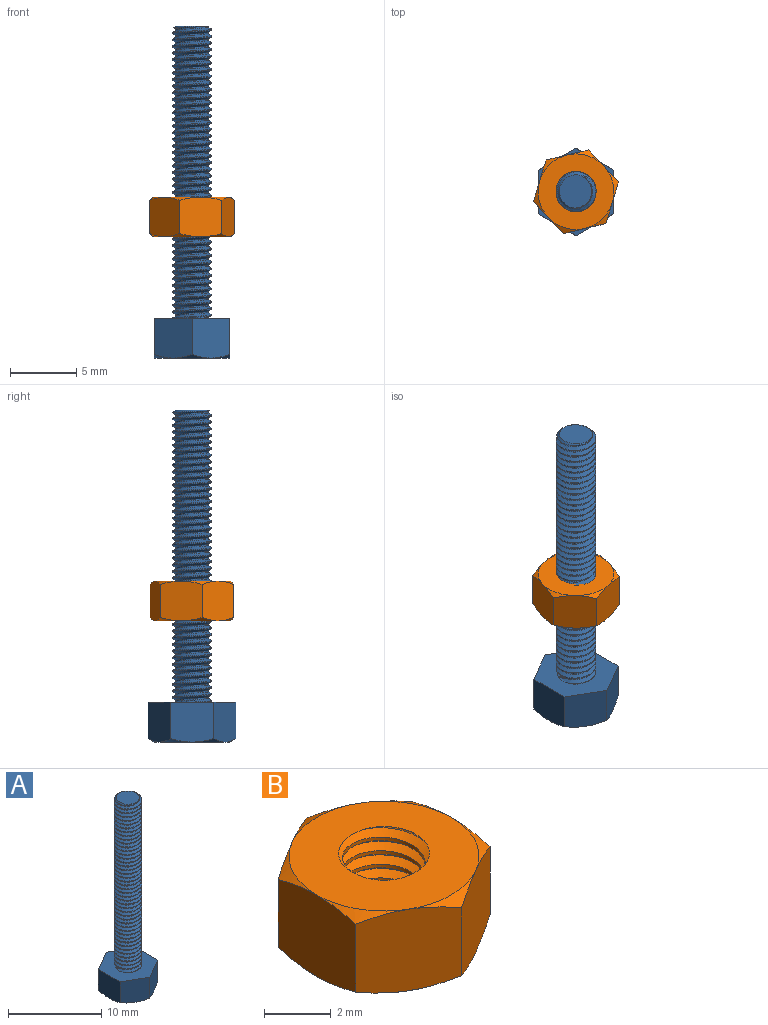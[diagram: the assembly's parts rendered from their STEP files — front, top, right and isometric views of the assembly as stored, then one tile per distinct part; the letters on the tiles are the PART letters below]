
ASSEMBLY  parts=2 mates=1
PART A: 20 faces, bbox 6.8x6.8x25.4 mm
  f0: cylinder r=1.5mm len=21.78mm, axis (0,0,-1), area -58.4mm2, adj f8,f17,f18,f19
  f1: plane 3.23x3.08mm, normal (0.5,0.87,0), area 9.6mm2, adj f2,f6,f7,f8,f10,f15
  f2: plane 3.23x3.08mm, normal (-0.5,0.86,0), area 9.6mm2, adj f1,f3,f7,f8,f14,f15
  f3: plane 3.52x3.23mm, normal (-1,0,0), area 9.6mm2, adj f2,f4,f7,f8,f13,f14
  f4: plane 3.23x3.08mm, normal (-0.5,-0.87,0), area 9.6mm2, adj f3,f5,f7,f8,f12,f13
  f5: plane 3.23x3.08mm, normal (0.5,-0.86,0), area 9.6mm2, adj f4,f6,f7,f8,f11,f12
  f6: plane 3.52x3.23mm, normal (1,0,0), area 9.6mm2, adj f1,f5,f7,f8,f10,f11
  f7: plane 5.71x5.7mm, normal (0,0,-1), area 25.6mm2, adj f1,f2,f3,f4,f5,f6,f10,f11
  f8: plane 6.72x5.85mm, normal (0,0,1), area 22.4mm2, adj f0,f1,f2,f3,f4,f5,f6,f16
  f9: plane 2.51x2.47mm, normal (0,0,1), area 4.8mm2, adj f16,f17,f18,f19
  f10: cone r=5.01mm half-angle=60deg, axis (0,0,1), area 0.7mm2, adj f1,f6,f7
  f11: cone r=5.01mm half-angle=60deg, axis (0,0,1), area 0.7mm2, adj f5,f6,f7
  f12: cone r=5.01mm half-angle=60deg, axis (0,0,1), area 0.7mm2, adj f4,f5,f7
  f13: cone r=5.01mm half-angle=60deg, axis (0,0,1), area 0.7mm2, adj f3,f4,f7
  f14: cone r=5.01mm half-angle=60deg, axis (0,0,1), area 0.7mm2, adj f2,f3,f7
  f15: cone r=5.01mm half-angle=60deg, axis (0,0,1), area 0.7mm2, adj f1,f2,f7
  f16: bspline ~22.38x2.84mm, area 46.8mm2, adj f8,f9,f17,f18
  f17: bspline ~22.41x3.46mm, area 117.7mm2, adj f0,f8,f9,f16,f19
  f18: bspline ~22.24x3.46mm, area 117.8mm2, adj f0,f8,f9,f16,f19
  f19: cone r=1.5mm half-angle=49.1deg, axis (0,0,-1), area 1.2mm2, adj f0,f9,f17,f18
PART B: 24 faces, bbox 6.9x6.9x3.7 mm
  f0: plane 5.84x5.84mm, normal (0,0,1), area 19.6mm2, adj f4,f5,f7,f9,f11,f13,f20,f21
  f1: plane 5.84x5.84mm, normal (0,0,-1), area 19.6mm2, adj f2,f3,f6,f8,f10,f12,f20,f21
  f2: cone r=2.85mm half-angle=60deg, axis (0,0,1), area 0.8mm2, adj f1,f14,f15
  f3: cone r=2.85mm half-angle=60deg, axis (0,0,1), area 0.8mm2, adj f1,f14,f19
  f4: cone r=2.85mm half-angle=60deg, axis (0,0,-1), area 0.8mm2, adj f0,f14,f15
  f5: cone r=2.85mm half-angle=60deg, axis (0,0,-1), area 0.8mm2, adj f0,f14,f19
  f6: cone r=2.85mm half-angle=60deg, axis (0,0,1), area 0.8mm2, adj f1,f15,f16
  f7: cone r=2.85mm half-angle=60deg, axis (0,0,-1), area 0.8mm2, adj f0,f15,f16
  f8: cone r=2.85mm half-angle=60deg, axis (0,0,1), area 0.8mm2, adj f1,f16,f17
  f9: cone r=2.85mm half-angle=60deg, axis (0,0,-1), area 0.8mm2, adj f0,f16,f17
  f10: cone r=2.85mm half-angle=60deg, axis (0,0,1), area 0.8mm2, adj f1,f17,f18
  f11: cone r=2.85mm half-angle=60deg, axis (0,0,-1), area 0.8mm2, adj f0,f17,f18
  f12: cone r=2.85mm half-angle=60deg, axis (0,0,1), area 0.8mm2, adj f1,f18,f19
  f13: cone r=2.85mm half-angle=60deg, axis (0,0,-1), area 0.8mm2, adj f0,f18,f19
  f14: plane 3.28x3.12mm, normal (0.5,-0.87,0), area 9.3mm2, adj f2,f3,f4,f5,f15,f19
  f15: plane 3.28x3.12mm, normal (-0.5,-0.87,0), area 9.3mm2, adj f2,f4,f6,f7,f14,f16
  f16: plane 3.56x3.27mm, normal (-1,0,0), area 9.3mm2, adj f6,f7,f8,f9,f15,f17
  f17: plane 3.28x3.12mm, normal (-0.5,0.87,0), area 9.3mm2, adj f8,f9,f10,f11,f16,f18
  f18: plane 3.28x3.12mm, normal (0.5,0.87,0), area 9.3mm2, adj f10,f11,f12,f13,f17,f19
  f19: plane 3.56x3.27mm, normal (1,0,0), area 9.3mm2, adj f3,f5,f12,f13,f14,f18
  f20: bspline ~3.51x3.32mm, area 16.3mm2, adj f0,f1,f22,f23
  f21: bspline ~3.51x3.41mm, area 16.3mm2, adj f0,f1,f22,f23
  f22: bspline ~3.56x3.23mm, area 4.2mm2, adj f0,f1,f20,f21
  f23: cylinder r=1.25mm len=3mm, axis (0,0,1), area 6.1mm2, adj f0,f1,f20,f21
PLACE A t=(12.16,8.71,-10.19)mm fixed
PLACE B rot(axis=(0,0,1),43.3deg) t=(12.16,8.71,-1.07)mm
MATE cylindrical B.f23 <-> A.f10  axis (0,0,-1) through (12.16,8.71,-1.07)mm
